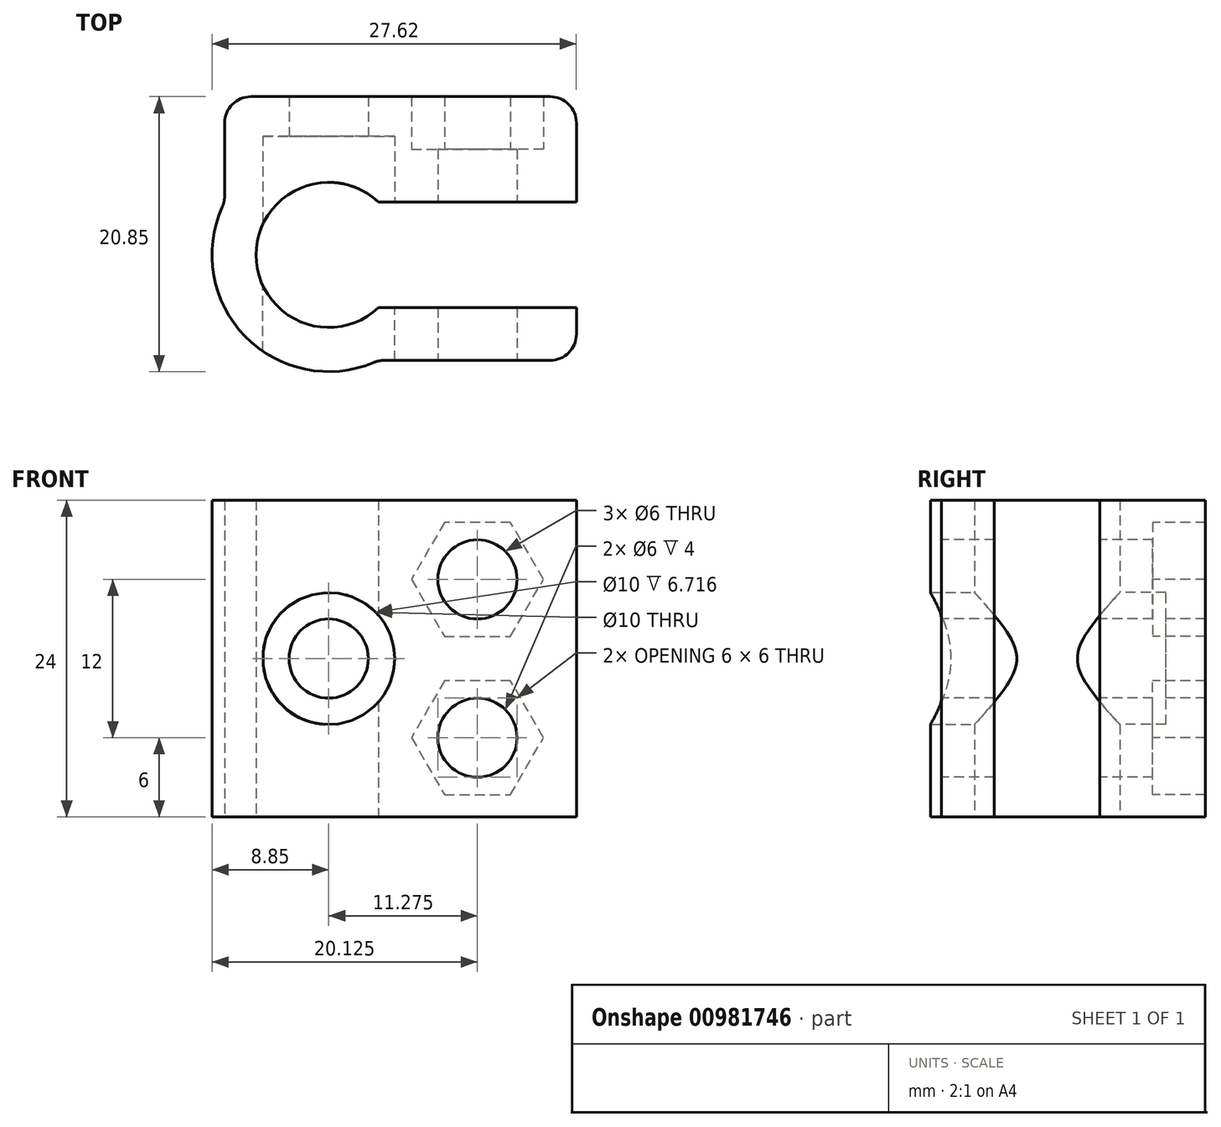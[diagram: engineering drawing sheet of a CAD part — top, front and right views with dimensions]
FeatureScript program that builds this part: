
annotation { "Feature Type Name" : "Feature", "Feature Type Description" : "" }
export const myFeature = defineFeature(function(context is Context, id is Id, definition is map)
    precondition{}
    {
        {
            var Q0;
            Q0=qCreatedBy(makeId("Top.planeOp"),FACE);
            var sketch = newSketch(context, id + "F0", { "sketchPlane" : qUnion([Q0])});
            skArc(sketch, "E0", {"start": v(3.77, 4) * mm, "mid": v(-5.5, 0) * mm, "end": v(3.77, -4) * mm});
            skLineSegment(sketch, "E1", {"start": v(3.77, -4) * mm, "end": v(18.77, -4) * mm});
            skLineSegment(sketch, "E2", {"start": v(18.77, -4) * mm, "end": v(18.77, -8) * mm});
            skLineSegment(sketch, "E3", {"start": v(18.77, -8) * mm, "end": v(3.77, -8) * mm});
            skLineSegment(sketch, "E4", {"start": v(3.77, 4) * mm, "end": v(18.77, 4) * mm});
            skLineSegment(sketch, "E5", {"start": v(18.77, 4) * mm, "end": v(18.77, 8) * mm});
            skArc(sketch, "E6", {"start": v(-7.89, 4) * mm, "mid": v(-6.34, -6.17) * mm, "end": v(3.77, -8) * mm});
            skLineSegment(sketch, "E7", {"start": v(3.77, -4) * mm, "end": v(3.77, -8) * mm, "construction": true});
            skLineSegment(sketch, "E8", {"start": v(3.77, 4) * mm, "end": v(-7.89, 4) * mm, "construction": true});
            skLineSegment(sketch, "E9", {"start": v(-7.89, 4) * mm, "end": v(-7.89, 12) * mm});
            skLineSegment(sketch, "E10", {"start": v(-7.89, 12) * mm, "end": v(3.77, 12) * mm});
            skLineSegment(sketch, "E11", {"start": v(3.77, 12) * mm, "end": v(18.77, 12) * mm});
            skLineSegment(sketch, "E12", {"start": v(18.77, 12) * mm, "end": v(18.77, 8) * mm});
            skPoint(sketch, "E13.orphan", {"position": v(3.77, 8) * mm});
            skSolve(sketch);
        }
        {
            var Q0;
            Q0=makeQuery(id+"F0.imprint","IMPRINT",FACE,{"disambiguationData":[TD([[makeQuery(id+"F0.imprint","IMPRINT",EDGE,{"derivedFrom":sQuery(id+"F0.wireOp",EDGE,"E0")}),-1.0]])]});
            extrude(context, id + "F1", {"entities" : qUnion([Q0]), "depth" : 24 * mm, "offsetDistance" : 25 * mm});
        }
        {
            var Q0;
            Q0=qCreatedBy(makeId("Front.planeOp"),FACE);
            var sketch = newSketch(context, id + "F2", { "sketchPlane" : qUnion([Q0])});
            skCircle(sketch, "E14", {"center": v(0, 12) * mm, "radius": 3 * mm});
            skCircle(sketch, "E15", {"center": v(11.27, 18) * mm, "radius": 3 * mm});
            skCircle(sketch, "E16", {"center": v(11.27, 6) * mm, "radius": 3 * mm});
            skLineSegment(sketch, "E17", {"start": v(11.27, 24) * mm, "end": v(11.27, 18) * mm, "construction": true});
            skLineSegment(sketch, "E18", {"start": v(11.27, 18) * mm, "end": v(11.27, 12) * mm, "construction": true});
            skLineSegment(sketch, "E19", {"start": v(11.27, 12) * mm, "end": v(11.27, 6) * mm, "construction": true});
            skLineSegment(sketch, "E20", {"start": v(11.27, 6) * mm, "end": v(11.27, 0) * mm, "construction": true});
            skCircle(sketch, "E21.cCircle", {"center": v(0, 12) * mm, "radius": 5 * mm});
            skLineSegment(sketch, "E21.0", {"start": v(-5, 12) * mm, "end": v(-2.5, 16.33) * mm});
            skLineSegment(sketch, "E21.1", {"start": v(-2.5, 16.33) * mm, "end": v(2.5, 16.33) * mm});
            skLineSegment(sketch, "E21.2", {"start": v(2.5, 16.33) * mm, "end": v(5, 12) * mm});
            skLineSegment(sketch, "E21.3", {"start": v(5, 12) * mm, "end": v(2.5, 7.67) * mm});
            skLineSegment(sketch, "E21.4", {"start": v(2.5, 7.67) * mm, "end": v(-2.5, 7.67) * mm});
            skLineSegment(sketch, "E21.5", {"start": v(-2.5, 7.67) * mm, "end": v(-5, 12) * mm});
            skCircle(sketch, "E22.cCircle", {"center": v(11.27, 18) * mm, "radius": 5 * mm, "construction": true});
            skLineSegment(sketch, "E22.0", {"start": v(16.27, 18) * mm, "end": v(13.77, 13.67) * mm});
            skLineSegment(sketch, "E22.1", {"start": v(13.77, 13.67) * mm, "end": v(8.77, 13.67) * mm});
            skLineSegment(sketch, "E22.2", {"start": v(8.77, 13.67) * mm, "end": v(6.27, 18) * mm});
            skLineSegment(sketch, "E22.3", {"start": v(6.27, 18) * mm, "end": v(8.77, 22.33) * mm});
            skLineSegment(sketch, "E22.4", {"start": v(8.77, 22.33) * mm, "end": v(13.77, 22.33) * mm});
            skLineSegment(sketch, "E22.5", {"start": v(13.77, 22.33) * mm, "end": v(16.27, 18) * mm});
            skCircle(sketch, "E23.cCircle", {"center": v(11.27, 6) * mm, "radius": 5 * mm, "construction": true});
            skLineSegment(sketch, "E23.0", {"start": v(6.27, 6) * mm, "end": v(8.77, 10.33) * mm});
            skLineSegment(sketch, "E23.1", {"start": v(8.77, 10.33) * mm, "end": v(13.77, 10.33) * mm});
            skLineSegment(sketch, "E23.2", {"start": v(13.77, 10.33) * mm, "end": v(16.27, 6) * mm});
            skLineSegment(sketch, "E23.3", {"start": v(16.27, 6) * mm, "end": v(13.77, 1.67) * mm});
            skLineSegment(sketch, "E23.4", {"start": v(13.77, 1.67) * mm, "end": v(8.77, 1.67) * mm});
            skLineSegment(sketch, "E23.5", {"start": v(8.77, 1.67) * mm, "end": v(6.27, 6) * mm});
            skSolve(sketch);
        }
        {
            var Q0;
            Q0=makeQuery(id+"F2.imprint","IMPRINT",FACE,{"disambiguationData":[TD([[makeQuery(id+"F2.imprint","IMPRINT",EDGE,{"derivedFrom":sQuery(id+"F2.wireOp",EDGE,"E16")}),1.0]])]});
            var Q1;
            Q1=makeQuery(id+"F2.imprint","IMPRINT",FACE,{"disambiguationData":[TD([[makeQuery(id+"F2.imprint","IMPRINT",EDGE,{"derivedFrom":sQuery(id+"F2.wireOp",EDGE,"E15")}),1.0]])]});
            var Q2;
            Q2=makeQuery(id+"F1.opExtrude","SWEPT_FACE",FACE,{"disambiguationData":[OSD([sQuery(id+"F0.wireOp",EDGE,"E3")])]});
            var Q3;
            Q3=makeQuery(id+"F1.opExtrude","SWEPT_BODY",BODY,{"disambiguationData":[OSD([sQuery(id+"F0.wireOp",EDGE,"E0"),sQuery(id+"F0.wireOp",EDGE,"E1"),sQuery(id+"F0.wireOp",EDGE,"E2"),sQuery(id+"F0.wireOp",EDGE,"E3"),sQuery(id+"F0.wireOp",EDGE,"E4"),sQuery(id+"F0.wireOp",EDGE,"E5"),sQuery(id+"F0.wireOp",EDGE,"GKUKXJLz-FTB8-EE2x-wA5D-qOMhcARyrjgv"),sQuery(id+"F0.wireOp",EDGE,"E6"),sQuery(id+"F0.wireOp",EDGE,"E9"),sQuery(id+"F0.wireOp",EDGE,"E10"),sQuery(id+"F0.wireOp",EDGE,"E11"),sQuery(id+"F0.wireOp",EDGE,"E12")])]});
            extrude(context, id + "F3", {"entities" : qUnion([Q0, Q1]), "operationType" : NewBodyOperationType.REMOVE, "oppositeDirection" : true, "depth" : 50 * mm, "endBoundEntityFace" : qUnion([Q2]), "endBoundEntityBody" : qUnion([Q3]), "offsetDistance" : 25 * mm, "symmetric" : true});
        }
        {
            var Q0;
            Q0=makeQuery(id+"F2.imprint","IMPRINT",FACE,{"disambiguationData":[TD([[makeQuery(id+"F2.imprint","IMPRINT",EDGE,{"derivedFrom":sQuery(id+"F2.wireOp",EDGE,"E15")}),-1.0]])]});
            var Q1;
            Q1=makeQuery(id+"F2.imprint","IMPRINT",FACE,{"disambiguationData":[TD([[makeQuery(id+"F2.imprint","IMPRINT",EDGE,{"derivedFrom":sQuery(id+"F2.wireOp",EDGE,"E16")}),-1.0]])]});
            extrude(context, id + "F4", {"entities" : qUnion([Q0, Q1]), "operationType" : NewBodyOperationType.REMOVE, "oppositeDirection" : true, "depth" : 25 * mm, "offsetDistance" : 25 * mm, "hasSecondDirection" : true, "secondDirectionOppositeDirection" : true, "secondDirectionDepth" : 8 * mm});
        }
        {
            var Q0;
            Q0=makeQuery(id+"F2.imprint","IMPRINT",FACE,{"disambiguationData":[TD([[makeQuery(id+"F2.imprint","IMPRINT",EDGE,{"derivedFrom":sQuery(id+"F2.wireOp",EDGE,"E14")}),1.0]])]});
            var Q1;
            Q1=sQuery(id+"F2.wireOp",EDGE,"E14");
            extrude(context, id + "F5", {"entities" : qUnion([Q0]), "operationType" : NewBodyOperationType.REMOVE, "surfaceEntities" : qUnion([Q1]), "oppositeDirection" : true, "depth" : 25 * mm, "offsetDistance" : 25 * mm});
        }
        {
            var Q0;
            Q0=makeQuery(id+"F2.imprint","IMPRINT",FACE,{"disambiguationData":[TD([[makeQuery(id+"F2.imprint","IMPRINT",EDGE,{"derivedFrom":sQuery(id+"F2.wireOp",EDGE,"E14")}),1.0]])]});
            var Q1;
            Q1=makeQuery(id+"F2.imprint","IMPRINT",FACE,{"disambiguationData":[TD([[makeQuery(id+"F2.imprint","IMPRINT",EDGE,{"derivedFrom":sQuery(id+"F2.wireOp",EDGE,"E14")}),-1.0]])]});
            var Q2;
            {var subQ0=sQuery(id+"F2.wireOp",EDGE,"E21.3");Q2=makeQuery(id+"F2.imprint","IMPRINT",FACE,{"disambiguationData":[TD([[makeQuery(id+"F2.imprint","IMPRINT",EDGE,{"derivedFrom":subQ0}),1.0]])]});}
            var Q3;
            {var subQ0=sQuery(id+"F2.wireOp",EDGE,"E21.2");Q3=makeQuery(id+"F2.imprint","IMPRINT",FACE,{"disambiguationData":[TD([[makeQuery(id+"F2.imprint","IMPRINT",EDGE,{"derivedFrom":subQ0}),1.0]])]});}
            var Q4;
            {var subQ0=sQuery(id+"F2.wireOp",EDGE,"E21.1");Q4=makeQuery(id+"F2.imprint","IMPRINT",FACE,{"disambiguationData":[TD([[makeQuery(id+"F2.imprint","IMPRINT",EDGE,{"derivedFrom":subQ0}),1.0]])]});}
            var Q5;
            {var subQ0=sQuery(id+"F2.wireOp",EDGE,"E21.0");Q5=makeQuery(id+"F2.imprint","IMPRINT",FACE,{"disambiguationData":[TD([[makeQuery(id+"F2.imprint","IMPRINT",EDGE,{"derivedFrom":subQ0}),1.0]])]});}
            var Q6;
            {var subQ0=sQuery(id+"F2.wireOp",EDGE,"E21.5");Q6=makeQuery(id+"F2.imprint","IMPRINT",FACE,{"disambiguationData":[TD([[makeQuery(id+"F2.imprint","IMPRINT",EDGE,{"derivedFrom":subQ0}),1.0]])]});}
            var Q7;
            {var subQ0=sQuery(id+"F2.wireOp",EDGE,"E21.4");Q7=makeQuery(id+"F2.imprint","IMPRINT",FACE,{"disambiguationData":[TD([[makeQuery(id+"F2.imprint","IMPRINT",EDGE,{"derivedFrom":subQ0}),1.0]])]});}
            extrude(context, id + "F6", {"entities" : qUnion([Q0, Q1, Q2, Q3, Q4, Q5, Q6, Q7]), "operationType" : NewBodyOperationType.REMOVE, "oppositeDirection" : true, "depth" : 9 * mm, "offsetDistance" : 25 * mm});
        }
        {
            var Q0;
            {var subQ0=sQuery(id+"F2.wireOp",EDGE,"E21.1");Q0=makeQuery(id+"F2.imprint","IMPRINT",FACE,{"disambiguationData":[TD([[makeQuery(id+"F2.imprint","IMPRINT",EDGE,{"derivedFrom":subQ0}),1.0]])]});}
            var Q1;
            Q1=makeQuery(id+"F2.imprint","IMPRINT",FACE,{"disambiguationData":[TD([[makeQuery(id+"F2.imprint","IMPRINT",EDGE,{"derivedFrom":sQuery(id+"F2.wireOp",EDGE,"E14")}),-1.0]])]});
            var Q2;
            {var subQ0=sQuery(id+"F2.wireOp",EDGE,"E21.2");Q2=makeQuery(id+"F2.imprint","IMPRINT",FACE,{"disambiguationData":[TD([[makeQuery(id+"F2.imprint","IMPRINT",EDGE,{"derivedFrom":subQ0}),1.0]])]});}
            var Q3;
            {var subQ0=sQuery(id+"F2.wireOp",EDGE,"E21.3");Q3=makeQuery(id+"F2.imprint","IMPRINT",FACE,{"disambiguationData":[TD([[makeQuery(id+"F2.imprint","IMPRINT",EDGE,{"derivedFrom":subQ0}),1.0]])]});}
            var Q4;
            {var subQ0=sQuery(id+"F2.wireOp",EDGE,"E21.4");Q4=makeQuery(id+"F2.imprint","IMPRINT",FACE,{"disambiguationData":[TD([[makeQuery(id+"F2.imprint","IMPRINT",EDGE,{"derivedFrom":subQ0}),1.0]])]});}
            var Q5;
            {var subQ0=sQuery(id+"F2.wireOp",EDGE,"E21.5");Q5=makeQuery(id+"F2.imprint","IMPRINT",FACE,{"disambiguationData":[TD([[makeQuery(id+"F2.imprint","IMPRINT",EDGE,{"derivedFrom":subQ0}),1.0]])]});}
            var Q6;
            {var subQ0=sQuery(id+"F2.wireOp",EDGE,"E21.0");Q6=makeQuery(id+"F2.imprint","IMPRINT",FACE,{"disambiguationData":[TD([[makeQuery(id+"F2.imprint","IMPRINT",EDGE,{"derivedFrom":subQ0}),1.0]])]});}
            var Q7;
            Q7=makeQuery(id+"F2.imprint","IMPRINT",FACE,{"disambiguationData":[TD([[makeQuery(id+"F2.imprint","IMPRINT",EDGE,{"derivedFrom":sQuery(id+"F2.wireOp",EDGE,"E14")}),1.0]])]});
            extrude(context, id + "F7", {"entities" : qUnion([Q0, Q1, Q2, Q3, Q4, Q5, Q6, Q7]), "operationType" : NewBodyOperationType.REMOVE, "depth" : 25 * mm, "offsetDistance" : 25 * mm});
        }
        {
            var Q0;
            Q0=makeQuery(id+"F1.opExtrude","SWEPT_EDGE",EDGE,{"disambiguationData":[OSD([sQuery(id+"F0.wireOp",EDGE,"E9"),sQuery(id+"F0.wireOp",EDGE,"E10")])]});
            var Q1;
            Q1=makeQuery(id+"F1.opExtrude","SWEPT_EDGE",EDGE,{"disambiguationData":[OSD([sQuery(id+"F0.wireOp",EDGE,"E6"),sQuery(id+"F0.wireOp",EDGE,"E9")])]});
            var Q2;
            Q2=makeQuery(id+"F1.opExtrude","SWEPT_EDGE",EDGE,{"disambiguationData":[OSD([sQuery(id+"F0.wireOp",EDGE,"E2"),sQuery(id+"F0.wireOp",EDGE,"E3")])]});
            var Q3;
            Q3=makeQuery(id+"F1.opExtrude","SWEPT_EDGE",EDGE,{"disambiguationData":[OSD([sQuery(id+"F0.wireOp",EDGE,"E11"),sQuery(id+"F0.wireOp",EDGE,"E12")])]});
            var Q4;
            Q4=makeQuery(id+"F1.opExtrude","SWEPT_EDGE",EDGE,{"disambiguationData":[OSD([sQuery(id+"F0.wireOp",EDGE,"E3"),sQuery(id+"F0.wireOp",EDGE,"E6")])]});
            fillet(context, id + "F8", {"entities" : qUnion([Q0, Q1, Q2, Q3, Q4]), "radius" : 2 * mm, "tangentPropagation" : true, "allowEdgeOverflow" : false});
        }
    });
